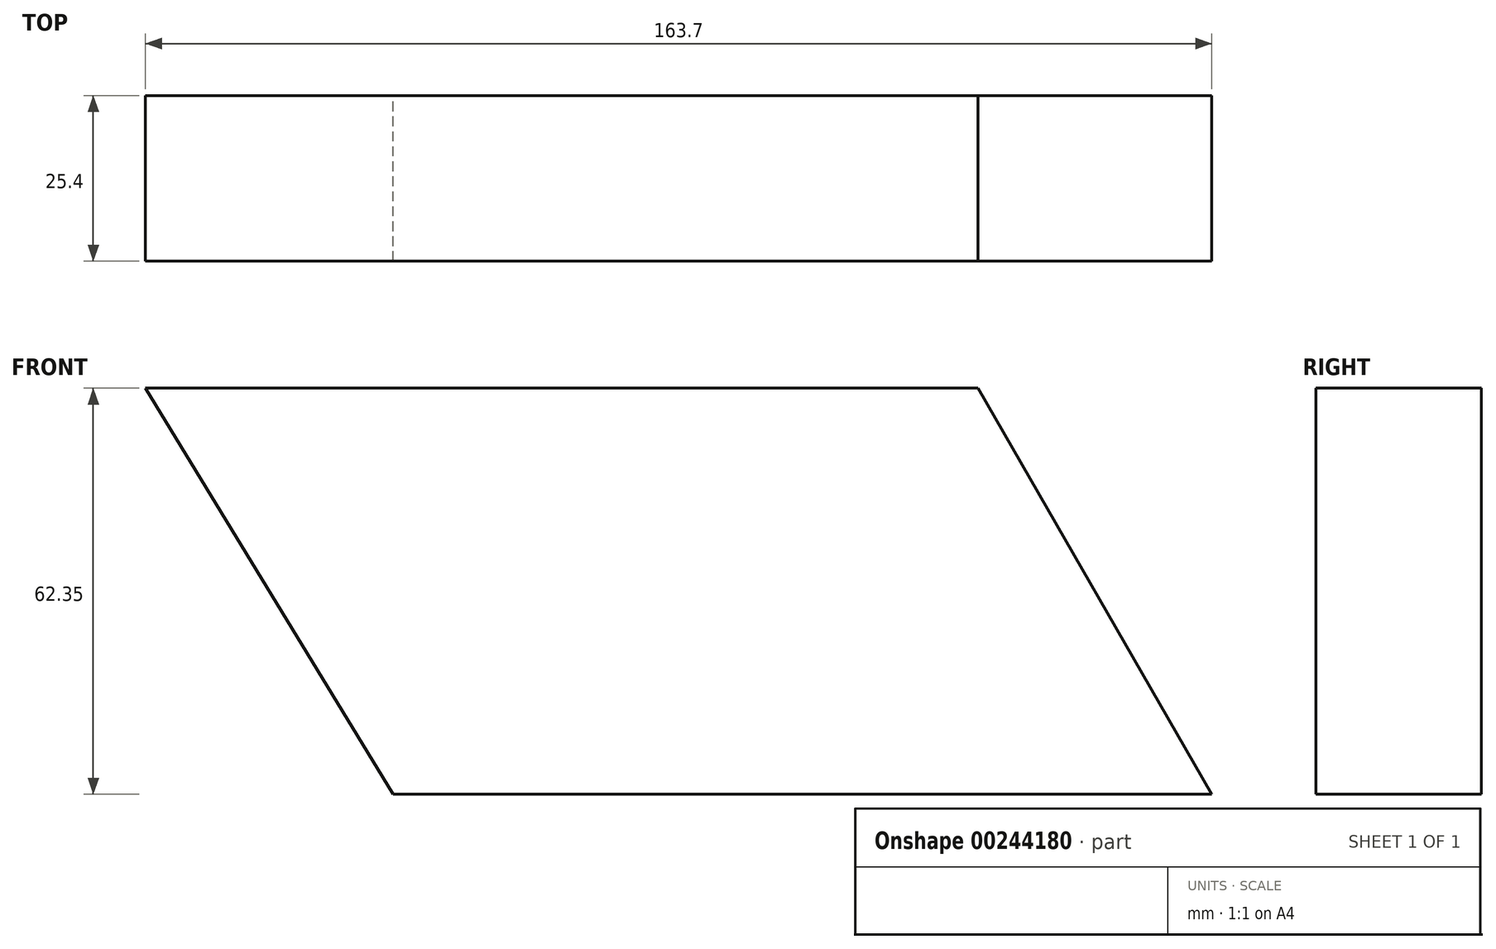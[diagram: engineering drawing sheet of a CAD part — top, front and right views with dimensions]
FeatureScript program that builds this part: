
annotation { "Feature Type Name" : "Feature", "Feature Type Description" : "" }
export const myFeature = defineFeature(function(context is Context, id is Id, definition is map)
    precondition{}
    {
        {
            var Q0;
            Q0=qCreatedBy(makeId("Front.planeOp"),FACE);
            var sketch = newSketch(context, id + "F0", { "sketchPlane" : qUnion([Q0])});
            skLineSegment(sketch, "E0", {"start": v(0, 0) * mm, "end": v(125.68, 0) * mm});
            skLineSegment(sketch, "E1", {"start": v(125.68, 0) * mm, "end": v(89.77, 62.35) * mm});
            skLineSegment(sketch, "E2", {"start": v(89.77, 62.35) * mm, "end": v(-38.02, 62.35) * mm});
            skLineSegment(sketch, "E3", {"start": v(-38.02, 62.35) * mm, "end": v(0, 0) * mm});
            skSolve(sketch);
        }
        {
            var Q0;
            Q0=makeQuery(id+"F0.imprint","IMPRINT",FACE,{"disambiguationData":[TD([[makeQuery(id+"F0.imprint","IMPRINT",EDGE,{"derivedFrom":sQuery(id+"F0.wireOp",EDGE,"E0")}),1.0]])]});
            extrude(context, id + "F1", {"entities" : qUnion([Q0]), "depth" : 25.4 * mm});
        }
    });
